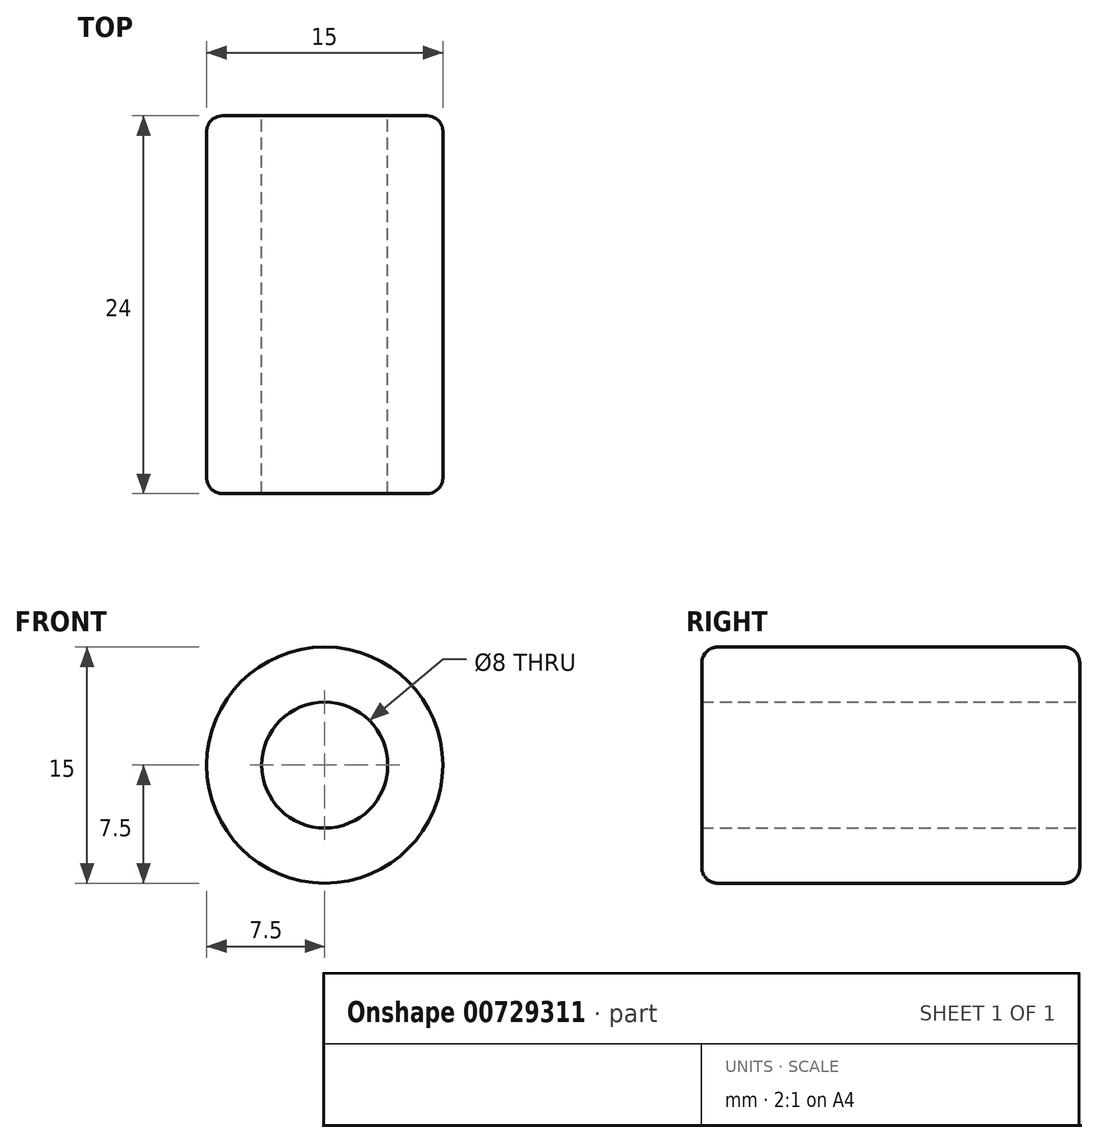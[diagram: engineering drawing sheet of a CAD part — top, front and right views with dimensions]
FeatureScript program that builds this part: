
annotation { "Feature Type Name" : "Feature", "Feature Type Description" : "" }
export const myFeature = defineFeature(function(context is Context, id is Id, definition is map)
    precondition{}
    {
        {
            var Q0;
            Q0=qCreatedBy(makeId("Front.planeOp"),FACE);
            var sketch = newSketch(context, id + "F0", { "sketchPlane" : qUnion([Q0])});
            skCircle(sketch, "E0", {"center": v(15, 15) * mm, "radius": 7.5 * mm});
            skCircle(sketch, "E1", {"center": v(15, 15) * mm, "radius": 4 * mm});
            skSolve(sketch);
        }
        {
            var Q0;
            Q0=makeQuery(id+"F0.imprint","IMPRINT",FACE,{"disambiguationData":[TD([[makeQuery(id+"F0.imprint","IMPRINT",EDGE,{"derivedFrom":sQuery(id+"F0.wireOp",EDGE,"E0")}),1.0]])]});
            extrude(context, id + "F1", {"entities" : qUnion([Q0]), "depth" : 24 * mm, "offsetDistance" : 25 * mm});
        }
        {
            var Q0;
            Q0=makeQuery(id+"F1.opExtrude","CAP_EDGE",EDGE,{"disambiguationData":[OSD([sQuery(id+"F0.wireOp",EDGE,"E0")])],"isStart":false});
            var Q1;
            Q1=makeQuery(id+"F1.opExtrude","CAP_EDGE",EDGE,{"disambiguationData":[OSD([sQuery(id+"F0.wireOp",EDGE,"E0")])],"isStart":true});
            fillet(context, id + "F2", {"entities" : qUnion([Q0, Q1]), "tangentPropagation" : true, "radius" : 1 * mm, "defaultsChanged" : true, "vertexSettings" : [], "allowEdgeOverflow" : false});
        }
    });
